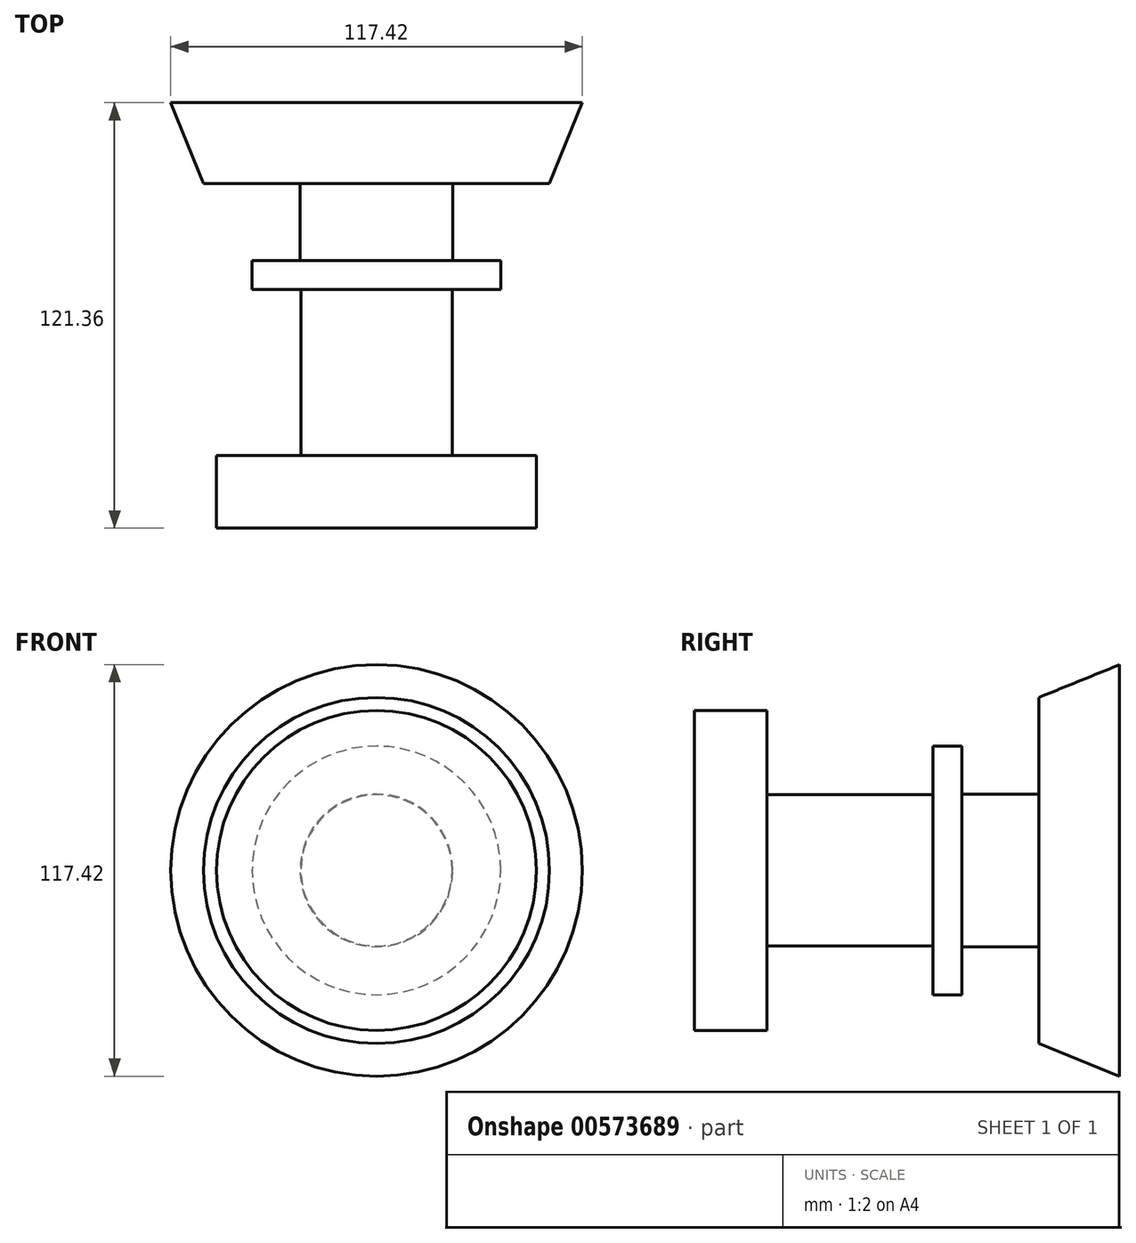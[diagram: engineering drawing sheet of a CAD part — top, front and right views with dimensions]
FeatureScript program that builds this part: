
annotation { "Feature Type Name" : "Feature", "Feature Type Description" : "" }
export const myFeature = defineFeature(function(context is Context, id is Id, definition is map)
    precondition{}
    {
        {
            var Q0;
            Q0=qCreatedBy(makeId("Top.planeOp"),FACE);
            var sketch = newSketch(context, id + "F0", { "sketchPlane" : qUnion([Q0])});
            skLineSegment(sketch, "E0", {"start": v(0, -76.34) * mm, "end": v(-45.64, -76.34) * mm});
            skLineSegment(sketch, "E1", {"start": v(-45.64, -76.34) * mm, "end": v(-45.64, -55.6) * mm});
            skLineSegment(sketch, "E2", {"start": v(-45.64, -55.6) * mm, "end": v(-21.58, -55.6) * mm});
            skLineSegment(sketch, "E3", {"start": v(-21.58, -55.6) * mm, "end": v(-21.58, -8.3) * mm});
            skLineSegment(sketch, "E4", {"start": v(-21.58, -8.3) * mm, "end": v(-35.48, -8.3) * mm});
            skLineSegment(sketch, "E5", {"start": v(-35.48, -8.3) * mm, "end": v(-35.48, 0) * mm});
            skLineSegment(sketch, "E6", {"start": v(-35.48, 0) * mm, "end": v(-21.78, 0) * mm});
            skLineSegment(sketch, "E7", {"start": v(-21.78, 0) * mm, "end": v(-21.78, 22) * mm});
            skLineSegment(sketch, "E8", {"start": v(-21.78, 22) * mm, "end": v(-49.37, 22) * mm});
            skLineSegment(sketch, "E9", {"start": v(-49.37, 22) * mm, "end": v(-58.71, 45.02) * mm});
            skLineSegment(sketch, "E10", {"start": v(-58.71, 45.02) * mm, "end": v(0, 45.02) * mm});
            skLineSegment(sketch, "E11", {"start": v(0, 45.02) * mm, "end": v(0, -76.34) * mm});
            skSolve(sketch);
        }
        {
            var Q0;
            Q0=makeQuery(id+"F0.imprint","IMPRINT",FACE,{"disambiguationData":[TD([[makeQuery(id+"F0.imprint","IMPRINT",EDGE,{"derivedFrom":sQuery(id+"F0.wireOp",EDGE,"E0")}),-1.0]])]});
            var Q1;
            Q1=sQuery(id+"F0.wireOp",EDGE,"E11");
            revolve(context, id + "F1", {"entities" : qUnion([Q0]), "axis" : qUnion([Q1]), "revolveType" : RevolveType.FULL});
        }
    });
